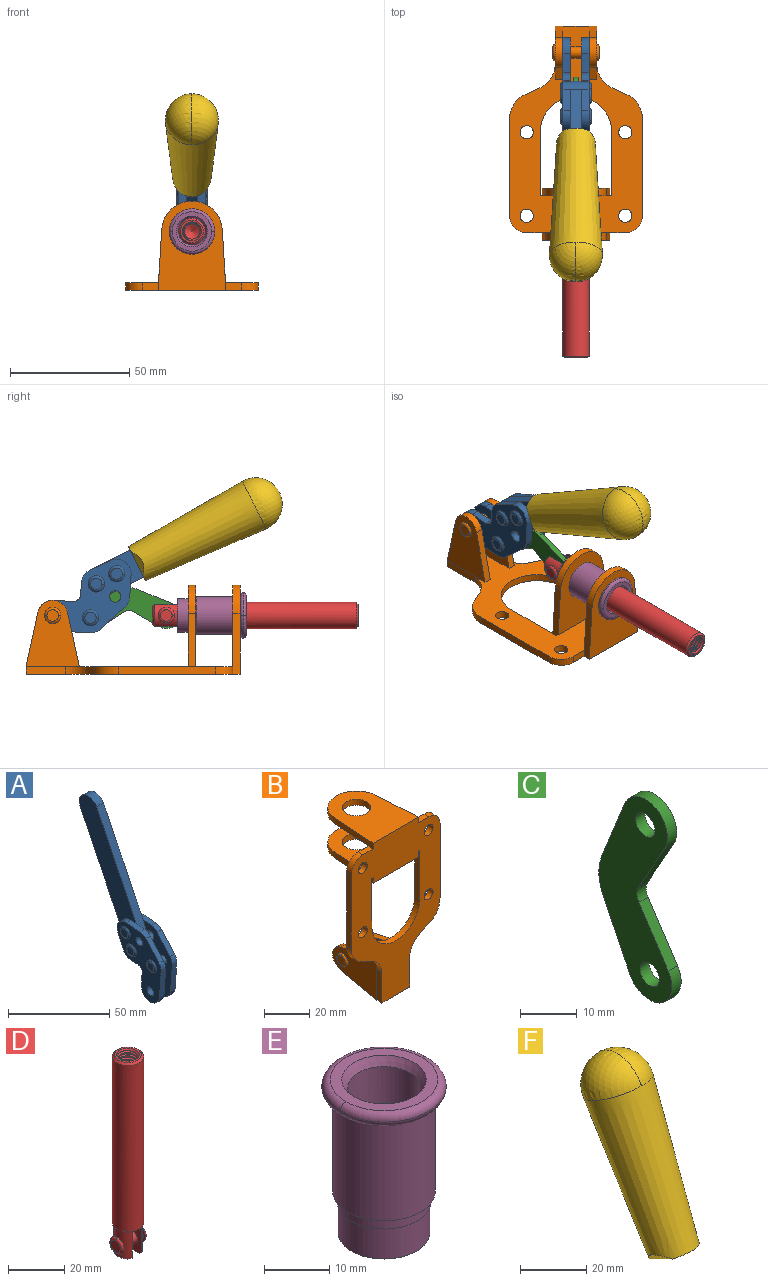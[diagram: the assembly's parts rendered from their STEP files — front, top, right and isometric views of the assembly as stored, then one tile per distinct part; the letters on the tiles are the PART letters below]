
ASSEMBLY  parts=6 mates=6
PART A: 59 faces, bbox 12.9x60.2x99.6 mm
  f0: torus R=2.39mm, axis (-1,0,0), area 14.9mm2, adj f20,f43,f51
  f1: torus R=2.39mm, axis (-1,0,0), area 14.9mm2, adj f19,f42,f51
  f2: torus R=2.39mm, axis (-1,0,0), area 14.9mm2, adj f18,f35,f51
  f3: torus R=2.39mm, axis (-1,0,0), area 14.9mm2, adj f14,f17,f23
  f4: torus R=2.39mm, axis (-1,0,0), area 14.9mm2, adj f13,f16,f23
  f5: torus R=2.39mm, axis (-1,0,0), area 14.9mm2, adj f12,f15,f23
  f6: cylinder r=2.39mm len=4.78mm, axis (1,0,0), area 46.5mm2, adj f48,f50,f51
  f7: cylinder r=2.39mm len=4.78mm, axis (1,0,0), area 46.5mm2, adj f50,f51
  f8: cylinder r=6.35mm len=12.68mm, axis (1,0,0), area 61.8mm2, adj f38,f39,f50,f51
  f9: cylinder r=2.39mm len=4.78mm, axis (-1,0,0), area 70.5mm2, adj f46,f50
  f10: cylinder r=2.39mm len=4.78mm, axis (-1,0,0), area 46.5mm2, adj f23,f45,f46
  f11: cylinder r=2.39mm len=4.78mm, axis (-1,0,0), area 46.5mm2, adj f23,f46
  f12: plane 4.78x4.78mm, normal (1,0,0), area 17.9mm2, adj f5,f15
  f13: plane 4.78x4.78mm, normal (1,0,0), area 17.9mm2, adj f4,f16
  f14: plane 4.78x4.78mm, normal (1,0,0), area 17.9mm2, adj f3,f17
  f15: torus R=2.39mm, axis (-1,0,0), area 14.9mm2, adj f5,f12,f23
  f16: torus R=2.39mm, axis (-1,0,0), area 14.9mm2, adj f4,f13,f23
  f17: torus R=2.39mm, axis (-1,0,0), area 14.9mm2, adj f3,f14,f23
  f18: plane 4.78x4.78mm, normal (-1,0,0), area 17.9mm2, adj f2,f35
  f19: plane 4.78x4.78mm, normal (-1,0,0), area 17.9mm2, adj f1,f42
  f20: plane 4.78x4.78mm, normal (-1,0,0), area 17.9mm2, adj f0,f43
  f21: plane 2.26x0.2mm, normal (1,0,0), area 0.2mm2, adj f31,f44
  f22: plane 2.26x0.2mm, normal (-1,0,0), area 0.2mm2, adj f41,f44
  f23: plane 39.37x30.77mm, normal (1,0,0), area 565.5mm2, adj f3,f4,f5,f10,f11,f15,f16,f17
  f24: cylinder r=6.1mm len=4.15mm, axis (-1,0,0), area 14.7mm2, adj f23,f25,f32,f46
  f25: plane 10.25x9.01mm, normal (0,-0.75,0.66), area 42.3mm2, adj f23,f24,f26,f46
  f26: cylinder r=6.35mm len=4.64mm, axis (-1,0,0), area 15.6mm2, adj f23,f25,f27,f46
  f27: plane 15.84x3.1mm, normal (0,-1,-0.07), area 49.2mm2, adj f23,f26,f28,f46
  f28: cylinder r=6.35mm len=12.68mm, axis (-1,0,0), area 61.8mm2, adj f23,f27,f29,f46
  f29: plane 8.11x3.1mm, normal (0,1,0.07), area 25.2mm2, adj f23,f28,f30,f46
  f30: cylinder r=3.05mm len=3.25mm, axis (-1,0,0), area 14.8mm2, adj f23,f29,f31,f46
  f31: plane 5.99x3.1mm, normal (0,0.07,-1), area 18.6mm2, adj f21,f23,f30,f44,f46
  f32: plane 9.5x3.1mm, normal (0,-0.07,1), area 29.5mm2, adj f23,f24,f33,f46,f47
  f33: cylinder r=6.1mm len=8.63mm, axis (-1,0,0), area 39.1mm2, adj f23,f32,f34,f47
  f34: plane 8.65x3.96mm, normal (0,0.91,-0.42), area 29.5mm2, adj f23,f33,f44,f47
  f35: torus R=2.39mm, axis (-1,0,0), area 14.9mm2, adj f2,f18,f51
  f36: plane 10.25x9.01mm, normal (0,-0.75,0.66), area 42.3mm2, adj f37,f49,f50,f51
  f37: cylinder r=6.35mm len=4.64mm, axis (1,0,0), area 15.6mm2, adj f36,f38,f50,f51
  f38: plane 15.84x3.1mm, normal (0,-1,-0.07), area 49.2mm2, adj f8,f37,f50,f51
  f39: plane 8.11x3.1mm, normal (0,1,0.07), area 25.2mm2, adj f8,f40,f50,f51
  f40: cylinder r=3.05mm len=3.25mm, axis (1,0,0), area 14.8mm2, adj f39,f41,f50,f51
  f41: plane 5.99x3.1mm, normal (0,0.07,-1), area 18.6mm2, adj f22,f40,f44,f50,f51
  f42: torus R=2.39mm, axis (-1,0,0), area 14.9mm2, adj f1,f19,f51
  f43: torus R=2.39mm, axis (-1,0,0), area 14.9mm2, adj f0,f20,f51
  f44: cylinder r=6.35mm len=12.12mm, axis (-1,0,0), area 128.9mm2, adj f21,f22,f23,f31,f34,f41,f46,f47
  f45: plane 2.65x1.35mm, normal (1,0,0), area 1mm2, adj f10,f55
  f46: plane 39.08x20.42mm, normal (-1,0,0), area 412.5mm2, adj f9,f10,f11,f24,f25,f26,f27,f28
  f47: plane 77.62x39.82mm, normal (1,0,0), area 850mm2, adj f32,f33,f34,f44,f53,f54,f55
  f48: plane 2.65x1.35mm, normal (-1,0,0), area 1mm2, adj f6,f55
  f49: cylinder r=6.1mm len=4.15mm, axis (1,0,0), area 14.7mm2, adj f36,f50,f51,f56
  f50: plane 39.08x20.42mm, normal (1,0,0), area 412.5mm2, adj f6,f7,f8,f9,f36,f37,f38,f39
  f51: plane 39.37x30.77mm, normal (-1,0,0), area 565.5mm2, adj f0,f1,f2,f6,f7,f8,f35,f36
  f52: plane 8.65x3.96mm, normal (0,0.91,-0.42), area 29.5mm2, adj f44,f51,f57,f58
  f53: plane 68.49x33.4mm, normal (0,0.9,-0.44), area 358.1mm2, adj f44,f47,f54,f58
  f54: cylinder r=6.35mm len=12.06mm, axis (1,0,0), area 93.7mm2, adj f47,f53,f55,f58
  f55: plane 68.49x33.4mm, normal (0,-0.9,0.44), area 358.1mm2, adj f44,f45,f46,f47,f48,f50,f54,f58
  f56: plane 9.5x3.1mm, normal (0,-0.07,1), area 29.5mm2, adj f49,f50,f51,f57,f58
  f57: cylinder r=6.1mm len=8.63mm, axis (1,0,0), area 39.1mm2, adj f51,f52,f56,f58
  f58: plane 77.62x39.82mm, normal (-1,0,0), area 850mm2, adj f44,f52,f53,f54,f55,f56,f57
PART B: 55 faces, bbox 55.7x37.4x89.8 mm
  f0: torus R=2.41mm, axis (-1,0,0), area 15mm2, adj f11,f15,f25
  f1: torus R=2.41mm, axis (-1,0,0), area 15mm2, adj f10,f12,f22
  f2: cylinder r=2.78mm len=5.56mm, axis (0,-1,0), area 54.2mm2, adj f30,f54
  f3: cylinder r=14.99mm len=29.97mm, axis (0,-1,0), area 145.9mm2, adj f30,f49,f53,f54
  f4: cylinder r=2.78mm len=5.56mm, axis (0,-1,0), area 54.2mm2, adj f30,f54
  f5: cylinder r=2.78mm len=5.56mm, axis (0,-1,0), area 54.2mm2, adj f30,f54
  f6: cylinder r=2.78mm len=5.56mm, axis (0,-1,0), area 54.2mm2, adj f30,f54
  f7: cylinder r=6.35mm len=12.7mm, axis (0,0,1), area 123.6mm2, adj f27,f51
  f8: cylinder r=6.35mm len=12.7mm, axis (0,0,-1), area 124.7mm2, adj f21,f35
  f9: cylinder r=2.41mm len=11.18mm, axis (-1,0,0), area 169.4mm2, adj f16,f19
  f10: plane 4.83x4.83mm, normal (1,0,0), area 18.3mm2, adj f1,f12
  f11: plane 4.83x4.83mm, normal (-1,0,0), area 18.3mm2, adj f0,f15
  f12: torus R=2.41mm, axis (-1,0,0), area 15mm2, adj f1,f10,f22
  f13: cylinder r=6.35mm len=12.41mm, axis (1,0,0), area 53.4mm2, adj f18,f19,f22,f23
  f14: cylinder r=6.35mm len=12.41mm, axis (-1,0,0), area 53.4mm2, adj f16,f17,f24,f25
  f15: torus R=2.41mm, axis (-1,0,0), area 15mm2, adj f0,f11,f25
  f16: plane 27.86x22.35mm, normal (1,0,0), area 425.4mm2, adj f9,f14,f17,f24,f30
  f17: plane 22.86x4.97mm, normal (0,0.21,0.98), area 72.5mm2, adj f14,f16,f25,f30
  f18: plane 22.86x4.97mm, normal (0,0.21,0.98), area 72.5mm2, adj f13,f19,f22,f30
  f19: plane 27.86x22.35mm, normal (-1,0,0), area 425.4mm2, adj f9,f13,f18,f23,f30
  f20: cylinder r=12.7mm len=25.35mm, axis (0,0,-1), area 119.8mm2, adj f21,f34,f35,f36
  f21: plane 34.21x28.07mm, normal (0,0,-1), area 702.4mm2, adj f8,f20,f30,f34,f36
  f22: plane 27.96x22.45mm, normal (1,0,0), area 407.2mm2, adj f1,f12,f13,f18,f23,f30,f42,f43
  f23: plane 22.86x4.97mm, normal (0,0.21,-0.98), area 72.5mm2, adj f13,f19,f22,f44
  f24: plane 22.86x4.97mm, normal (0,0.21,-0.98), area 72.5mm2, adj f14,f16,f25,f44
  f25: plane 27.86x22.35mm, normal (-1,0,0), area 407.1mm2, adj f0,f14,f15,f17,f24,f30,f45,f46
  f26: plane 3.1x0.95mm, normal (0,0,-1), area 2.7mm2, adj f30,f49,f50,f54
  f27: plane 34.21x28.07mm, normal (0,0,1), area 702.4mm2, adj f7,f28,f30,f50,f52
  f28: cylinder r=12.7mm len=25.35mm, axis (0,0,1), area 118.8mm2, adj f27,f50,f51,f52
  f29: plane 3.1x0.95mm, normal (0,0,-1), area 2.7mm2, adj f30,f52,f53,f54
  f30: plane 86.54x55.63mm, normal (0,1,0), area 2362.9mm2, adj f2,f3,f4,f5,f6,f16,f17,f18
  f31: plane 40.56x3.1mm, normal (-1,0,0), area 125.7mm2, adj f30,f32,f48,f54
  f32: cylinder r=7.11mm len=7.11mm, axis (0,-1,0), area 34.6mm2, adj f30,f31,f33,f54
  f33: plane 6.67x3.1mm, normal (0,0,1), area 20.4mm2, adj f30,f32,f34,f54
  f34: plane 25.39x3.13mm, normal (-1,0.06,0), area 79.5mm2, adj f20,f21,f33,f35,f54
  f35: plane 37.31x28.45mm, normal (0,0,1), area 789.9mm2, adj f8,f20,f34,f36,f54
  f36: plane 25.39x3.13mm, normal (1,0.06,0), area 79.5mm2, adj f20,f21,f35,f37,f54
  f37: plane 6.67x3.1mm, normal (0,0,1), area 20.4mm2, adj f30,f36,f38,f54
  f38: cylinder r=7.11mm len=7.11mm, axis (0,-1,0), area 34.6mm2, adj f30,f37,f39,f54
  f39: plane 40.56x3.1mm, normal (1,0,0), area 125.7mm2, adj f30,f38,f40,f54
  f40: cylinder r=11.18mm len=10.16mm, axis (0,-1,0), area 39.5mm2, adj f30,f39,f41,f54
  f41: plane 6.09x3.1mm, normal (0.42,0,-0.91), area 20.8mm2, adj f30,f40,f42,f54
  f42: cylinder r=11.18mm len=9.41mm, axis (0,-1,0), area 37.2mm2, adj f22,f30,f41,f43,f54
  f43: plane 16.5x3.1mm, normal (1,0,0), area 51.1mm2, adj f22,f42,f44,f54
  f44: plane 17.37x3.1mm, normal (0,0,-1), area 53.8mm2, adj f23,f24,f30,f43,f45,f54
  f45: plane 16.5x3.1mm, normal (-1,0,0), area 51.1mm2, adj f25,f44,f46,f54
  f46: cylinder r=11.18mm len=9.41mm, axis (0,-1,0), area 37.2mm2, adj f25,f30,f45,f47,f54
  f47: plane 6.09x3.1mm, normal (-0.42,0,-0.91), area 20.8mm2, adj f30,f46,f48,f54
  f48: cylinder r=11.18mm len=10.16mm, axis (0,-1,0), area 39.5mm2, adj f30,f31,f47,f54
  f49: plane 26.54x3.1mm, normal (-1,0,0), area 82.3mm2, adj f3,f26,f30,f54
  f50: plane 25.39x3.1mm, normal (1,0.06,0), area 78.8mm2, adj f26,f27,f28,f51,f54
  f51: plane 37.31x28.45mm, normal (0,0,-1), area 789.9mm2, adj f7,f28,f50,f52,f54
  f52: plane 25.39x3.1mm, normal (-1,0.06,0), area 78.8mm2, adj f27,f28,f29,f51,f54
  f53: plane 26.54x3.1mm, normal (1,0,0), area 82.3mm2, adj f3,f29,f30,f54
  f54: plane 89.66x55.63mm, normal (0,-1,0), area 2678.5mm2, adj f2,f3,f4,f5,f6,f26,f29,f31
PART C: 12 faces, bbox 2.3x18.2x42.8 mm
  f0: cylinder r=2.4mm len=4.8mm, axis (1,0,0), area 34.9mm2, adj f4,f11
  f1: cylinder r=10.41mm len=8.47mm, axis (1,0,0), area 20.2mm2, adj f4,f9,f10,f11
  f2: cylinder r=3.05mm len=3.16mm, axis (1,0,0), area 7.7mm2, adj f4,f6,f7,f11
  f3: cylinder r=2.4mm len=4.8mm, axis (1,0,0), area 34.9mm2, adj f4,f11
  f4: plane 42.81x18.23mm, normal (-1,0,0), area 414.1mm2, adj f0,f1,f2,f3,f5,f6,f7,f8
  f5: cylinder r=5.54mm len=10.67mm, axis (1,0,0), area 41.8mm2, adj f4,f6,f10,f11
  f6: plane 11.66x6.53mm, normal (0,-0.87,-0.49), area 30.9mm2, adj f2,f4,f5,f11
  f7: plane 11.17x7.33mm, normal (0,-0.84,0.55), area 30.9mm2, adj f2,f4,f8,f11
  f8: cylinder r=5.54mm len=10.51mm, axis (1,0,0), area 41.8mm2, adj f4,f7,f9,f11
  f9: plane 13.67x6.67mm, normal (0,0.9,-0.44), area 35.1mm2, adj f1,f4,f8,f11
  f10: plane 14.1x5.7mm, normal (0,0.93,0.37), area 35.1mm2, adj f1,f4,f5,f11
  f11: plane 42.81x18.23mm, normal (1,0,0), area 414.1mm2, adj f0,f1,f2,f3,f5,f6,f7,f8
PART D: 48 faces, bbox 12.6x11.1x86.1 mm
  f0: torus R=2.41mm, axis (-1,0,0), area 15mm2, adj f30,f32,f34
  f1: torus R=2.41mm, axis (-1,0,0), area 15mm2, adj f29,f31,f33
  f2: cylinder r=5.54mm len=72.39mm, axis (0,0,1), area 2518.5mm2, adj f3,f4,f42,f43
  f3: cone r=5.54mm half-angle=45deg, axis (0,0,1), area 7.6mm2, adj f2,f5,f41
  f4: cone r=5.54mm half-angle=45deg, axis (0,0,-1), area 34.9mm2, adj f2,f39
  f5: cylinder r=5.08mm len=11.48mm, axis (0,0,1), area 108.3mm2, adj f3,f7,f8,f41
  f6: cylinder r=2.41mm len=4.83mm, axis (-1,0,0), area 71.2mm2, adj f40,f41
  f7: cylinder r=2.41mm len=4.83mm, axis (-1,0,0), area 7.6mm2, adj f5,f34
  f8: cone r=5.08mm half-angle=45deg, axis (0,0,1), area 10.6mm2, adj f5,f37,f41
  f9: cone r=3.98mm half-angle=45deg, axis (0,0,1), area 17.6mm2, adj f27,f39,f45,f46,f47
  f10: cylinder r=2.41mm len=4.83mm, axis (-1,0,0), area 7.6mm2, adj f33,f38
  f11: cylinder r=3.2mm len=6.4mm, axis (0,0,1), area 78.4mm2, adj f12,f28,f44,f45,f47
  f12: cylinder r=3.2mm len=6.4mm, axis (0,0,1), area 10.5mm2, adj f11,f13,f45,f47
  f13: cylinder r=3.2mm len=6.4mm, axis (0,0,1), area 10.5mm2, adj f12,f14,f45,f47
  f14: cylinder r=3.2mm len=6.4mm, axis (0,0,1), area 10.5mm2, adj f13,f15,f45,f47
  f15: cylinder r=3.2mm len=6.4mm, axis (0,0,1), area 10.5mm2, adj f14,f16,f45,f47
  f16: cylinder r=3.2mm len=6.4mm, axis (0,0,1), area 10.5mm2, adj f15,f17,f45,f47
  f17: cylinder r=3.2mm len=6.4mm, axis (0,0,1), area 10.5mm2, adj f16,f18,f45,f47
  f18: cylinder r=3.2mm len=6.4mm, axis (0,0,1), area 10.5mm2, adj f17,f19,f45,f47
  f19: cylinder r=3.2mm len=6.4mm, axis (0,0,1), area 10.5mm2, adj f18,f20,f45,f47
  f20: cylinder r=3.2mm len=6.4mm, axis (0,0,1), area 10.5mm2, adj f19,f21,f45,f47
  f21: cylinder r=3.2mm len=6.4mm, axis (0,0,1), area 10.5mm2, adj f20,f22,f45,f47
  f22: cylinder r=3.2mm len=6.4mm, axis (0,0,1), area 10.5mm2, adj f21,f23,f45,f47
  f23: cylinder r=3.2mm len=6.4mm, axis (0,0,1), area 10.5mm2, adj f22,f24,f45,f47
  f24: cylinder r=3.2mm len=6.4mm, axis (0,0,1), area 10.5mm2, adj f23,f25,f45,f47
  f25: cylinder r=3.2mm len=6.4mm, axis (0,0,1), area 10.5mm2, adj f24,f26,f45,f47
  f26: cylinder r=3.2mm len=6.4mm, axis (0,0,1), area 10.5mm2, adj f25,f27,f45,f47
  f27: cylinder r=3.2mm len=6.4mm, axis (0,0,1), area 7.4mm2, adj f9,f26,f45,f47
  f28: cone r=3.2mm half-angle=60deg, axis (0,0,1), area 37.2mm2, adj f11
  f29: plane 4.83x4.83mm, normal (-1,0,0), area 18.3mm2, adj f1,f31
  f30: plane 4.83x4.83mm, normal (1,0,0), area 18.3mm2, adj f0,f32
  f31: torus R=2.41mm, axis (-1,0,0), area 15mm2, adj f1,f29,f33
  f32: torus R=2.41mm, axis (-1,0,0), area 15mm2, adj f0,f30,f34
  f33: plane 6.83x6.83mm, normal (1,0,0), area 18.3mm2, adj f1,f10,f31
  f34: plane 6.83x6.83mm, normal (-1,0,0), area 18.3mm2, adj f0,f7,f32
  f35: cone r=5.08mm half-angle=45deg, axis (0,0,1), area 10.6mm2, adj f36,f38,f40
  f36: plane 7.25x1.97mm, normal (0,0,-1), area 10mm2, adj f35,f40
  f37: plane 7.25x1.97mm, normal (0,0,-1), area 10mm2, adj f8,f41
  f38: cylinder r=5.08mm len=11.48mm, axis (0,0,1), area 108.3mm2, adj f10,f35,f40,f42
  f39: plane 9.55x9.55mm, normal (0,0,1), area 22mm2, adj f4,f9
  f40: plane 12.76x10.09mm, normal (1,0,0), area 95.7mm2, adj f6,f35,f36,f38,f42,f43
  f41: plane 12.76x10.09mm, normal (-1,0,0), area 95.7mm2, adj f3,f5,f6,f8,f37,f43
  f42: cone r=5.54mm half-angle=45deg, axis (0,0,1), area 7.6mm2, adj f2,f38,f40
  f43: plane 11.07x4.7mm, normal (0,0,-1), area 50.4mm2, adj f2,f40,f41
  f44: plane 0.89x0.62mm, normal (-1,0,0), area 0.3mm2, adj f11,f45,f46,f47
  f45: bspline ~24.8x7.63mm, area 266.6mm2, adj f9,f11,f12,f13,f14,f15,f16,f17
  f46: bspline ~24.87x7.63mm, area 73.6mm2, adj f9,f44,f45,f47
  f47: bspline ~24.98x7.63mm, area 272.5mm2, adj f9,f11,f12,f13,f14,f15,f16,f17
PART E: 15 faces, bbox 20.6x20.6x28.7 mm
  f0: torus R=8.26mm, axis (0,0,1), area 56.8mm2, adj f1,f10,f12
  f1: torus R=8.26mm, axis (0,0,1), area 56.8mm2, adj f0,f6,f13
  f2: cylinder r=5.59mm len=25.91mm, axis (0,0,1), area 909.6mm2, adj f3,f4
  f3: cone r=6.86mm half-angle=45deg, axis (0,0,-1), area 70.2mm2, adj f2,f14
  f4: cone r=6.47mm half-angle=30deg, axis (0,0,1), area 66.7mm2, adj f2,f13
  f5: cylinder r=7.04mm len=14.07mm, axis (0,0,1), area 252.6mm2, adj f11,f14
  f6: torus R=8.26mm, axis (0,0,1), area 56.8mm2, adj f1,f12,f13
  f7: cylinder r=7.16mm len=14.33mm, axis (0,0,1), area 91.5mm2, adj f9,f11
  f8: cylinder r=7.86mm len=18.42mm, axis (0,0,1), area 909.6mm2, adj f9,f10
  f9: plane 15.72x15.72mm, normal (0,0,-1), area 33mm2, adj f7,f8
  f10: plane 16.51x16.51mm, normal (0,0,-1), area 19.9mm2, adj f0,f8,f12
  f11: plane 14.33x14.33mm, normal (0,0,-1), area 5.7mm2, adj f5,f7
  f12: torus R=8.26mm, axis (0,0,1), area 56.8mm2, adj f0,f6,f10
  f13: plane 16.51x16.51mm, normal (0,0,1), area 82.7mm2, adj f1,f4,f6
  f14: plane 14.07x14.07mm, normal (0,0,-1), area 7.8mm2, adj f3,f5
PART F: 11 faces, bbox 22.3x42.6x64.5 mm
  f0: sphere r=11.13mm, area 411.4mm2, adj f1,f8
  f1: cone r=11.11mm half-angle=3.3deg, axis (0,0.44,0.9), area 3251.8mm2, adj f0,f7,f8,f9,f10
  f2: cylinder r=6.16mm len=11.7mm, axis (1,0,0), area 89.5mm2, adj f3,f4,f5,f6
  f3: plane 60.23x36.75mm, normal (-1,0,0), area 763.6mm2, adj f2,f4,f6,f10
  f4: plane 51.37x25.05mm, normal (0,0.9,-0.44), area 264.2mm2, adj f2,f3,f5,f10
  f5: plane 60.23x36.75mm, normal (1,0,0), area 763.6mm2, adj f2,f4,f6,f10
  f6: plane 51.37x25.05mm, normal (0,-0.9,0.44), area 264.2mm2, adj f2,f3,f5,f10
  f7: plane 9.95x5.95mm, normal (0.71,-0.31,-0.64), area 25.8mm2, adj f1,f10
  f8: sphere r=11.13mm, area 411.4mm2, adj f0,f1
  f9: plane 9.95x5.95mm, normal (-0.71,-0.31,-0.64), area 25.8mm2, adj f1,f10
  f10: plane 14.27x11.38mm, normal (0,-0.44,-0.9), area 106.7mm2, adj f1,f3,f4,f5,f6,f7,f9
PLACE A rot(axis=(1,0,0),89.5deg) t=(0,8.91,0.3)mm
PLACE B rot(axis=(1,0,0),90deg) t=(0,9.14,0)mm fixed
PLACE C rot(axis=(1,0,0),90.3deg) t=(0,9.24,0.07)mm
PLACE D rot(axis=(1,0,0),90deg) t=(0,9.13,0)mm
PLACE E rot(axis=(1,0,0),90deg) t=(0,9.14,0)mm
PLACE F rot(axis=(1,0,0),89.5deg) t=(-0.04,8.91,0.3)mm
MATE revolute C.f3 <-> A.f4  axis (1,0,0) through (0,25.39,23.65)mm
MATE fastened E.f2 <-> B.f7  axis (0,1,0) through (0,-37.25,24.61)mm
MATE revolute C.f5 <-> D.f6  axis (1,0,0) through (0,-6.35,24.61)mm
MATE revolute A.f7 <-> B.f0  axis (-1,0,0) through (0,41.23,24.61)mm
MATE slider D.f2 <-> B.f7  axis (0,-1,0) through (0,-49.66,24.61)mm
MATE fastened A.f54 <-> F.f2  axis (-1,0,0) through (-2.35,-45.19,71.86)mm
